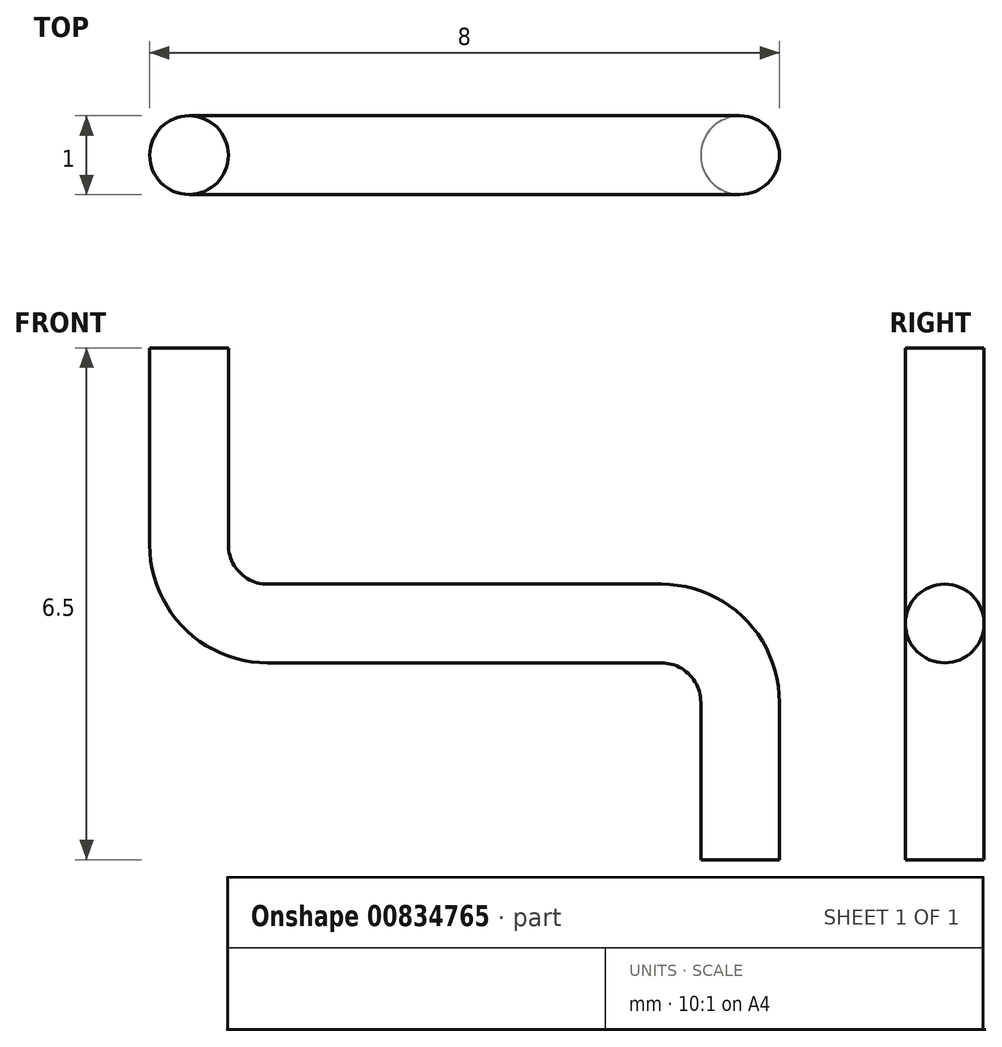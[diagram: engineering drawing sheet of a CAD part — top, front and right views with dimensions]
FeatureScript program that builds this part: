
annotation { "Feature Type Name" : "Feature", "Feature Type Description" : "" }
export const myFeature = defineFeature(function(context is Context, id is Id, definition is map)
    precondition{}
    {
        {
            var Q0;
            Q0=qCreatedBy(makeId("Front.planeOp"),FACE);
            var sketch = newSketch(context, id + "F0", { "sketchPlane" : qUnion([Q0])});
            skLineSegment(sketch, "E0", {"start": v(0, 0) * mm, "end": v(0, -2.5) * mm});
            skArc(sketch, "E1", {"start": v(0, -2.5) * mm, "mid": v(0.3, -3.2) * mm, "end": v(1, -3.5) * mm});
            skLineSegment(sketch, "E2", {"start": v(1, -3.5) * mm, "end": v(6, -3.5) * mm});
            skArc(sketch, "E3", {"start": v(6, -3.5) * mm, "mid": v(6.7, -3.8) * mm, "end": v(7, -4.5) * mm});
            skLineSegment(sketch, "E4", {"start": v(7, -4.5) * mm, "end": v(7, -6.5) * mm});
            skSolve(sketch);
        }
        {
            var Q0;
            Q0=qCreatedBy(makeId("Top.planeOp"),FACE);
            var sketch = newSketch(context, id + "F1", { "sketchPlane" : qUnion([Q0])});
            skCircle(sketch, "E5", {"center": v(0, 0) * mm, "radius": 0.5 * mm});
            skSolve(sketch);
        }
        {
            var Q0;
            Q0=makeQuery(id+"F1.imprint","IMPRINT",FACE,{"disambiguationData":[TD([[makeQuery(id+"F1.imprint","IMPRINT",EDGE,{"derivedFrom":sQuery(id+"F1.wireOp",EDGE,"E5")}),1.0]])]});
            var Q1;
            Q1=sQuery(id+"F0.wireOp",EDGE,"E0");
            var Q2;
            Q2=sQuery(id+"F0.wireOp",EDGE,"E1");
            var Q3;
            Q3=sQuery(id+"F0.wireOp",EDGE,"E2");
            var Q4;
            Q4=sQuery(id+"F0.wireOp",EDGE,"E3");
            var Q5;
            Q5=sQuery(id+"F0.wireOp",EDGE,"E4");
            sweep(context, id + "F2", {"profiles" : qUnion([Q0]), "path" : qUnion([Q1, Q2, Q3, Q4, Q5])});
        }
    });
